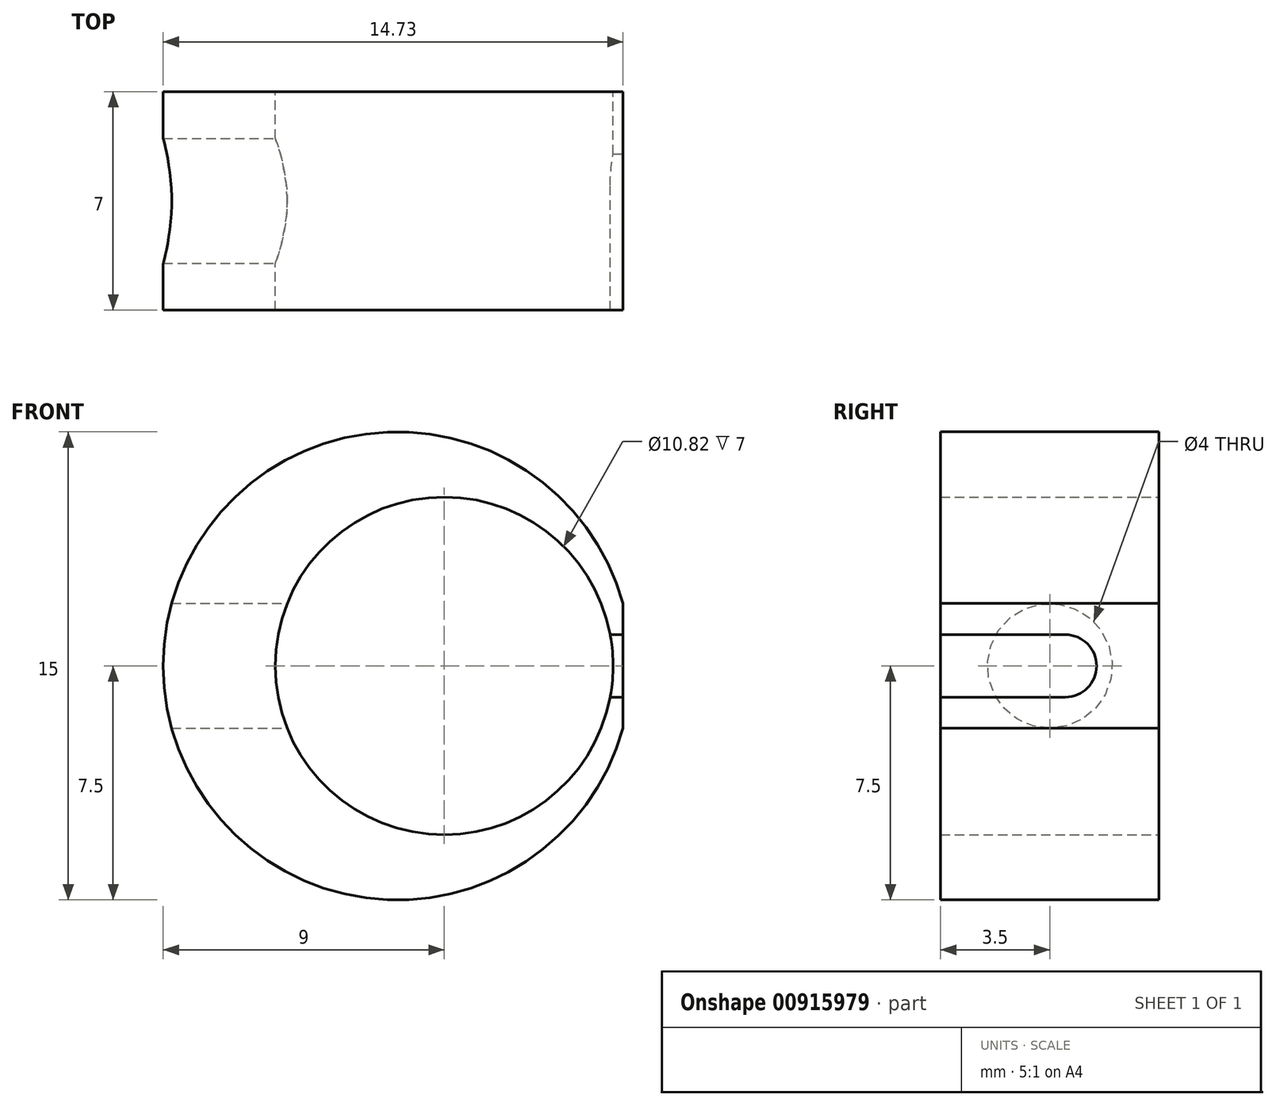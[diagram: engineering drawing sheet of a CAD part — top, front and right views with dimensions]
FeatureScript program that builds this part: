
annotation { "Feature Type Name" : "Feature", "Feature Type Description" : "" }
export const myFeature = defineFeature(function(context is Context, id is Id, definition is map)
    precondition{}
    {
        {
            var Q0;
            Q0=qCreatedBy(makeId("Front.planeOp"),FACE);
            var sketch = newSketch(context, id + "F0", { "sketchPlane" : qUnion([Q0])});
            skArc(sketch, "E0", {"start": v(7.23, 2) * mm, "mid": v(-7.5, 0) * mm, "end": v(7.23, -2) * mm});
            skArc(sketch, "E1", {"start": v(6.82, 1) * mm, "mid": v(-3.91, 0) * mm, "end": v(6.82, -1) * mm});
            skLineSegment(sketch, "E2", {"start": v(6.82, 1) * mm, "end": v(7.23, 1) * mm});
            skLineSegment(sketch, "E3", {"start": v(6.82, -1) * mm, "end": v(7.23, -1) * mm});
            skLineSegment(sketch, "E4.bottom", {"start": v(6.13, 2) * mm, "end": v(6.53, 2) * mm, "construction": true});
            skLineSegment(sketch, "E4.top", {"start": v(6.13, -2) * mm, "end": v(6.53, -2) * mm, "construction": true});
            skLineSegment(sketch, "E4.left", {"start": v(6.13, 2) * mm, "end": v(6.13, -2) * mm, "construction": true});
            skLineSegment(sketch, "E4.right", {"start": v(6.53, 2) * mm, "end": v(6.53, -2) * mm, "construction": true});
            skLineSegment(sketch, "E5", {"start": v(6.53, 2) * mm, "end": v(7.23, 2) * mm, "construction": true});
            skArc(sketch, "E6", {"start": v(6.82, 1) * mm, "mid": v(6.91, 0) * mm, "end": v(6.82, -1) * mm});
            skLineSegment(sketch, "E7", {"start": v(7.23, 3.32) * mm, "end": v(7.23, 1) * mm});
            skLineSegment(sketch, "E8", {"start": v(7.23, -1) * mm, "end": v(7.23, -3.4) * mm});
            skLineSegment(sketch, "E9", {"start": v(7.23, 1) * mm, "end": v(7.23, -1) * mm});
            skSolve(sketch);
        }
        {
            assignVariable(context, id + "F1", {"name" : "screw", "anyValue" : 4});
        }
        {
            assignVariable(context, id + "F2", {"name" : "min_wall", "anyValue" : 1.5});
        }
        {
            var Q0;
            Q0=makeQuery(id+"F0.imprint","IMPRINT",FACE,{"disambiguationData":[TD([[makeQuery(id+"F0.imprint","IMPRINT",EDGE,{"derivedFrom":sQuery(id+"F0.wireOp",EDGE,"E0")}),1.0]])]});
            var Q1;
            Q1=makeQuery(id+"F0.imprint","IMPRINT",FACE,{"disambiguationData":[TD([[makeQuery(id+"F0.imprint","IMPRINT",EDGE,{"derivedFrom":sQuery(id+"F0.wireOp",EDGE,"E2")}),-1.0]])]});
            extrude(context, id + "F3", {"entities" : qUnion([Q0, Q1]), "depth" : (getVariable(context, 'screw') + getVariable(context, 'min_wall') * 2) * mm, "offsetDistance" : 25 * mm});
        }
        {
            var Q0;
            Q0=qCreatedBy(makeId("Right.planeOp"),FACE);
            var sketch = newSketch(context, id + "F4", { "sketchPlane" : qUnion([Q0])});
            skCircle(sketch, "E10", {"center": v(-3.5, 0) * mm, "radius": 2 * mm});
            skSolve(sketch);
        }
        {
            var Q0;
            Q0=qSketchRegion(id+"F4",true);
            var Q1;
            Q1=makeQuery(id+"F3.opExtrude","SWEPT_FACE",FACE,{"disambiguationData":[OSD([sQuery(id+"F0.wireOp",EDGE,"E0")])]});
            var Q2;
            Q2=makeQuery(id+"F3.opExtrude","SWEPT_BODY",BODY,{"disambiguationData":[OSD([sQuery(id+"F0.wireOp",EDGE,"E0"),sQuery(id+"F0.wireOp",EDGE,"E1"),sQuery(id+"F0.wireOp",EDGE,"E2"),sQuery(id+"F0.wireOp",EDGE,"E3")])]});
            extrude(context, id + "F5", {"entities" : qUnion([Q0]), "operationType" : NewBodyOperationType.REMOVE, "endBound" : BoundingType.UP_TO_SURFACE, "oppositeDirection" : true, "depth" : 25 * mm, "endBoundEntityFace" : qUnion([Q1]), "endBoundEntityBody" : qUnion([Q2]), "offsetDistance" : 25 * mm});
        }
        {
            var Q0;
            Q0=makeQuery(id+"F3.opExtrude","SWEPT_FACE",FACE,{"disambiguationData":[OSD([sQuery(id+"F0.wireOp",EDGE,"E7"),sQuery(id+"F0.wireOp",EDGE,"E8"),sQuery(id+"F0.wireOp",EDGE,"E9")])]});
            var sketch = newSketch(context, id + "F6", { "sketchPlane" : qUnion([Q0])});
            skLineSegment(sketch, "E11", {"start": v(-7, -1) * mm, "end": v(-3, -1) * mm});
            skLineSegment(sketch, "E12", {"start": v(-7, 1) * mm, "end": v(-3, 1) * mm});
            skLineSegment(sketch, "E13", {"start": v(-3, -1) * mm, "end": v(-3, 1) * mm, "construction": true});
            skArc(sketch, "E14", {"start": v(-3, -1) * mm, "mid": v(-2, 0) * mm, "end": v(-3, 1) * mm});
            skLineSegment(sketch, "E15", {"start": v(-3, -1) * mm, "end": v(0, -1) * mm, "construction": true});
            skLineSegment(sketch, "E16", {"start": v(-3, 1) * mm, "end": v(0, 1) * mm, "construction": true});
            skSolve(sketch);
        }
        {
            var Q0;
            {var subQ0=sQuery(id+"F6.wireOp",EDGE,"E11");Q0=makeQuery(id+"F6.imprint","IMPRINT",FACE,{"disambiguationData":[TD([[makeQuery(id+"F6.imprint","IMPRINT",EDGE,{"derivedFrom":subQ0}),1.0]])]});}
            var Q1;
            Q1=makeQuery(id+"F3.opExtrude","SWEPT_FACE",FACE,{"disambiguationData":[OSD([sQuery(id+"F0.wireOp",EDGE,"E1"),sQuery(id+"F0.wireOp",EDGE,"E6")])]});
            extrude(context, id + "F7", {"entities" : qUnion([Q0]), "operationType" : NewBodyOperationType.REMOVE, "endBound" : BoundingType.UP_TO_SURFACE, "oppositeDirection" : true, "depth" : 25 * mm, "endBoundEntityFace" : qUnion([Q1]), "offsetDistance" : 25 * mm});
        }
    });
